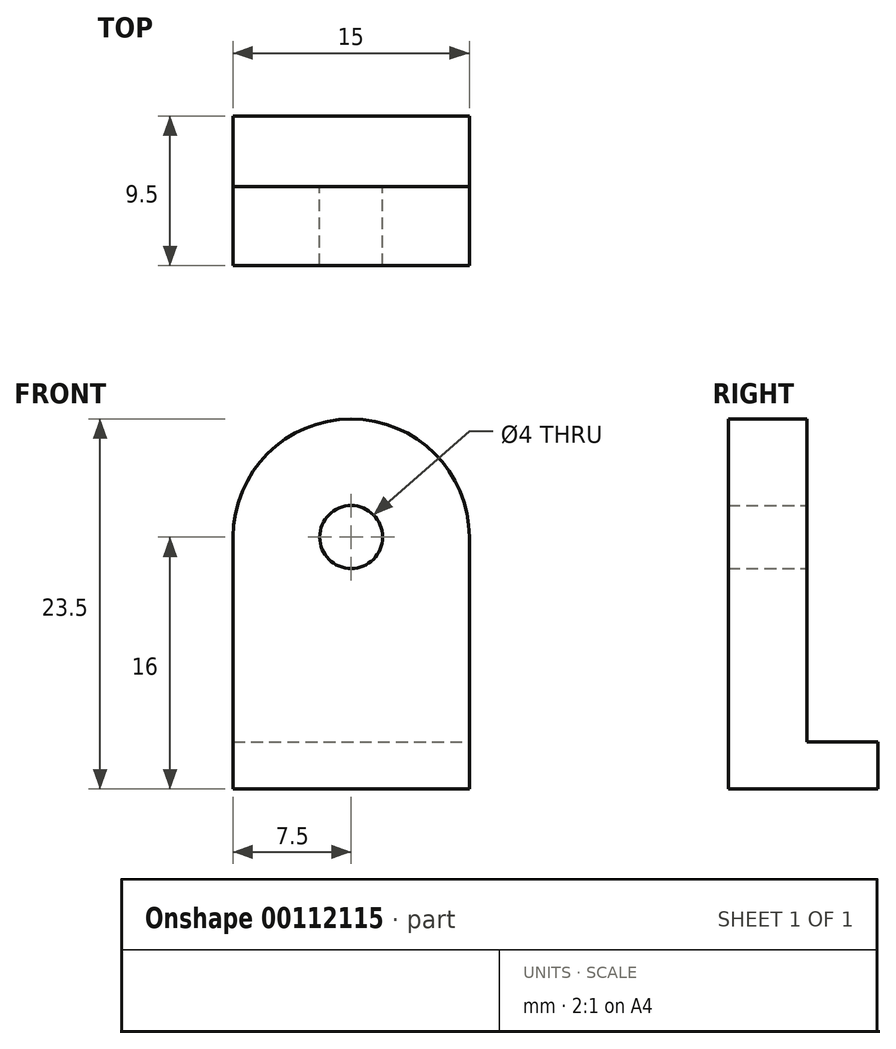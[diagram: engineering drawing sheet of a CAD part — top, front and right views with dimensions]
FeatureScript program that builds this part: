
annotation { "Feature Type Name" : "Feature", "Feature Type Description" : "" }
export const myFeature = defineFeature(function(context is Context, id is Id, definition is map)
    precondition{}
    {
        {
            var Q0;
            Q0=qCreatedBy(makeId("Front.planeOp"),FACE);
            var sketch = newSketch(context, id + "F0", { "sketchPlane" : qUnion([Q0])});
            skLineSegment(sketch, "E0", {"start": v(0, 0) * mm, "end": v(0, 3) * mm});
            skLineSegment(sketch, "E1", {"start": v(0, 3) * mm, "end": v(15, 3) * mm});
            skLineSegment(sketch, "E2", {"start": v(15, 3) * mm, "end": v(15, 0) * mm});
            skLineSegment(sketch, "E3", {"start": v(15, 0) * mm, "end": v(0, 0) * mm});
            skPoint(sketch, "E4.start.orphan", {"position": v(2, 8) * mm});
            skPoint(sketch, "E5.start.orphan", {"position": v(13, 8) * mm});
            skSolve(sketch);
        }
        {
            var Q0;
            Q0 = qSketchRegion(id + "F0", true);
            extrude(context, id + "F1", {"entities" : qUnion([Q0]), "depth" : 4.5 * mm});
        }
        {
            var Q0;
            Q0=makeQuery(id+"F1.opExtrude","CAP_FACE",FACE,{"disambiguationData":[OSD([sQuery(id+"F0.wireOp",EDGE,"E0"),sQuery(id+"F0.wireOp",EDGE,"Abgn2Ydg-IVdf-Kwdx-ycjH-zDiYzNPH7PMc"),sQuery(id+"F0.wireOp",EDGE,"E4"),sQuery(id+"F0.wireOp",EDGE,"E1"),sQuery(id+"F0.wireOp",EDGE,"AVEDbV4H-eFEq-pFAH-CVrt-FNd9JxGG6l8F"),sQuery(id+"F0.wireOp",EDGE,"E5"),sQuery(id+"F0.wireOp",EDGE,"E2"),sQuery(id+"F0.wireOp",EDGE,"E3")])],"isStart":false});
            var sketch = newSketch(context, id + "F2", { "sketchPlane" : qUnion([Q0])});
            skCircle(sketch, "E6", {"center": v(7.5, 16) * mm, "radius": 2 * mm});
            skPoint(sketch, "E6.centerSnap0", {"position": v(7.5, 3) * mm});
            skArc(sketch, "E7", {"start": v(15, 16) * mm, "mid": v(7.5, 23.5) * mm, "end": v(0, 16) * mm});
            skLineSegment(sketch, "E8", {"start": v(0, 16) * mm, "end": v(0, 0) * mm});
            skLineSegment(sketch, "E9", {"start": v(15, 16) * mm, "end": v(15, 0) * mm});
            skLineSegment(sketch, "E10", {"start": v(15, 0) * mm, "end": v(0, 0) * mm});
            skSolve(sketch);
        }
        {
            var Q0;
            Q0 = qSketchRegion(id + "F2", true);
            extrude(context, id + "F3", {"entities" : qUnion([Q0]), "operationType" : NewBodyOperationType.ADD, "depth" : 5 * mm});
        }
    });
